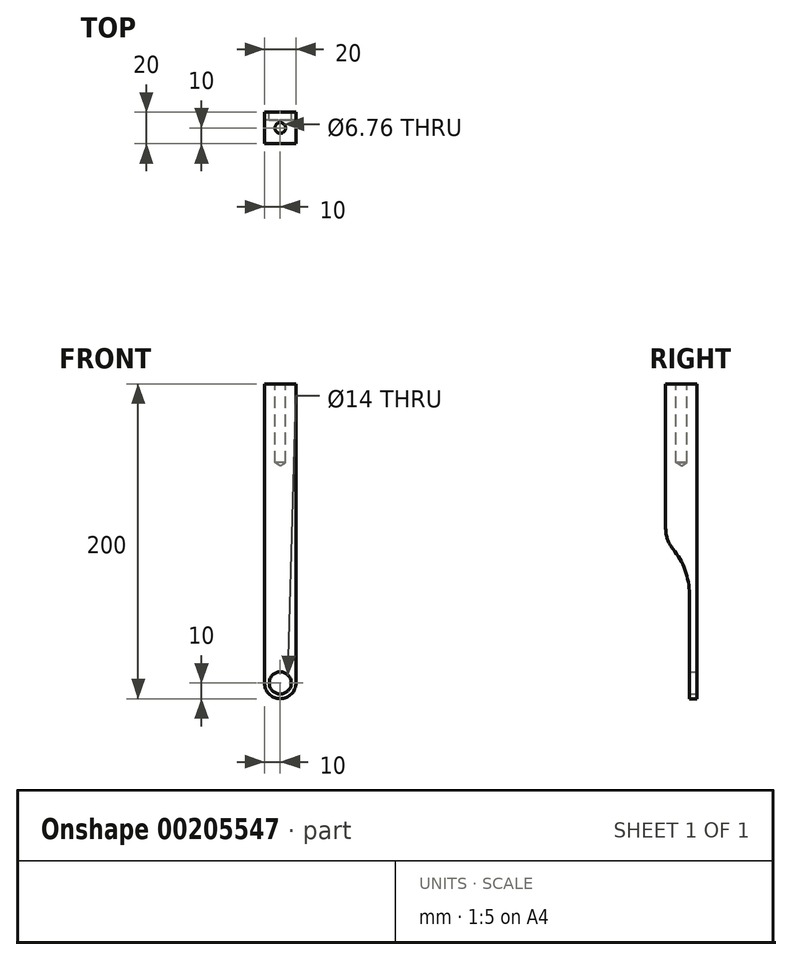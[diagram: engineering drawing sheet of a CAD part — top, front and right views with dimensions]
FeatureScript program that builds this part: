
annotation { "Feature Type Name" : "Feature", "Feature Type Description" : "" }
export const myFeature = defineFeature(function(context is Context, id is Id, definition is map)
    precondition{}
    {
        {
            var Q0;
            Q0=qCreatedBy(makeId("Front.planeOp"),FACE);
            var sketch = newSketch(context, id + "F0", { "sketchPlane" : qUnion([Q0])});
            skLineSegment(sketch, "E0.bottom", {"start": v(0, 0) * mm, "end": v(20, 0) * mm});
            skLineSegment(sketch, "E0.top", {"start": v(0, 200) * mm, "end": v(20, 200) * mm});
            skLineSegment(sketch, "E0.left", {"start": v(0, 0) * mm, "end": v(0, 200) * mm});
            skLineSegment(sketch, "E0.right", {"start": v(20, 0) * mm, "end": v(20, 200) * mm});
            skSolve(sketch);
        }
        {
            var Q0;
            Q0=qSketchRegion(id+"F0",true);
            extrude(context, id + "F1", {"entities" : qUnion([Q0]), "depth" : 20 * mm});
        }
        {
            var Q0;
            Q0=makeQuery(id+"F1.opExtrude","SWEPT_FACE",FACE,{"disambiguationData":[OSD([sQuery(id+"F0.wireOp",EDGE,"E0.right")])]});
            var sketch = newSketch(context, id + "F2", { "sketchPlane" : qUnion([Q0])});
            skLineSegment(sketch, "E1.bottom", {"start": v(-20, 0) * mm, "end": v(-5, 0) * mm});
            skLineSegment(sketch, "E1.top", {"start": v(-20, 100) * mm, "end": v(-5, 100) * mm});
            skLineSegment(sketch, "E1.left", {"start": v(-20, 0) * mm, "end": v(-20, 100) * mm});
            skLineSegment(sketch, "E1.right", {"start": v(-5, 0) * mm, "end": v(-5, 100) * mm});
            skSolve(sketch);
        }
        {
            var Q0;
            Q0=makeQuery(id+"F2.imprint","IMPRINT",FACE,{"disambiguationData":[TD([[makeQuery(id+"F2.imprint","IMPRINT",EDGE,{"derivedFrom":sQuery(id+"F2.wireOp",EDGE,"E1.bottom")}),1.0]])]});
            extrude(context, id + "F3", {"entities" : qUnion([Q0]), "operationType" : NewBodyOperationType.REMOVE, "oppositeDirection" : true, "depth" : 20 * mm});
        }
        {
            var Q0;
            Q0=makeQuery(id+"F1.opExtrude","CAP_FACE",FACE,{"disambiguationData":[OSD([sQuery(id+"F0.wireOp",EDGE,"E0.bottom"),sQuery(id+"F0.wireOp",EDGE,"E0.top"),sQuery(id+"F0.wireOp",EDGE,"E0.left"),sQuery(id+"F0.wireOp",EDGE,"E0.right")])],"isStart":true});
            var sketch = newSketch(context, id + "F4", { "sketchPlane" : qUnion([Q0])});
            skCircle(sketch, "E2", {"center": v(-10, 10) * mm, "radius": 10 * mm});
            skPoint(sketch, "E2.centerSnap0", {"position": v(-10, 0) * mm});
            skSolve(sketch);
        }
        {
            var Q0;
            {var subQ0=sQuery(id+"F4.wireOp",EDGE,"E2");var subQ1=makeQuery(id+"F1.opExtrude","CAP_EDGE",EDGE,{"disambiguationData":[OSD([sQuery(id+"F0.wireOp",EDGE,"E0.left")])],"isStart":true});var subQ2=makeQuery(id+"F4.imprint","INTERSECT",VERTEX,{"derivedFrom":[subQ1,subQ0]});Q0=makeQuery(id+"F4.imprint","IMPRINT",FACE,{"disambiguationData":[TD([[makeQuery(id+"F4.imprint","IMPRINT",EDGE,{"disambiguationData":[TD([[subQ2,1.0]])],"derivedFrom":subQ0}),-1.0]])]});}
            var Q1;
            {var subQ0=sQuery(id+"F4.wireOp",EDGE,"E2");var subQ1=makeQuery(id+"F1.opExtrude","CAP_EDGE",EDGE,{"disambiguationData":[OSD([sQuery(id+"F0.wireOp",EDGE,"E0.right")])],"isStart":true});var subQ2=makeQuery(id+"F4.imprint","INTERSECT",VERTEX,{"derivedFrom":[subQ1,subQ0]});Q1=makeQuery(id+"F4.imprint","IMPRINT",FACE,{"disambiguationData":[TD([[makeQuery(id+"F4.imprint","IMPRINT",EDGE,{"disambiguationData":[TD([[subQ2,-1.0]])],"derivedFrom":subQ0}),-1.0]])]});}
            var Q2;
            Q2=makeQuery(id+"F1.opExtrude","SWEPT_EDGE",EDGE,{"disambiguationData":[OSD([sQuery(id+"F0.wireOp",EDGE,"E0.bottom"),sQuery(id+"F0.wireOp",EDGE,"E0.left")])]});
            sweep(context, id + "F5", {"operationType" : NewBodyOperationType.REMOVE, "profiles" : qUnion([Q0, Q1]), "path" : qUnion([Q2])});
        }
        {
            var Q0;
            Q0=makeQuery(id+"F1.opExtrude","CAP_FACE",FACE,{"disambiguationData":[OSD([sQuery(id+"F0.wireOp",EDGE,"E0.bottom"),sQuery(id+"F0.wireOp",EDGE,"E0.top"),sQuery(id+"F0.wireOp",EDGE,"E0.left"),sQuery(id+"F0.wireOp",EDGE,"E0.right")])],"isStart":true});
            var sketch = newSketch(context, id + "F6", { "sketchPlane" : qUnion([Q0])});
            skCircle(sketch, "E3", {"center": v(-10, 10) * mm, "radius": 7 * mm});
            skSolve(sketch);
        }
        {
            var Q0;
            Q0=qSketchRegion(id+"F6",true);
            extrude(context, id + "F7", {"entities" : qUnion([Q0]), "operationType" : NewBodyOperationType.REMOVE, "endBound" : BoundingType.THROUGH_ALL, "oppositeDirection" : true, "depth" : 25 * mm});
        }
        {
            var Q0;
            Q0=makeQuery(id+"F3.boolean.opBoolean","COPY",EDGE,{"derivedFrom":makeQuery(id+"F3.opExtrude","SWEPT_EDGE",EDGE,{"disambiguationData":[OSD([sQuery(id+"F2.wireOp",EDGE,"E1.top"),sQuery(id+"F2.wireOp",EDGE,"E1.right")])]})});
            fillet(context, id + "F8", {"entities" : qUnion([Q0]), "radius" : 45 * mm, "tangentPropagation" : true, "allowEdgeOverflow" : false});
        }
        {
            var Q0;
            Q0=makeQuery(id+"F8.opFillet","BLEND_EDGE",EDGE,{"blendedFrom":[makeQuery(id+"F3.boolean.opBoolean","COPY",EDGE,{"derivedFrom":makeQuery(id+"F3.opExtrude","SWEPT_EDGE",EDGE,{"disambiguationData":[OSD([sQuery(id+"F2.wireOp",EDGE,"E1.top"),sQuery(id+"F2.wireOp",EDGE,"E1.right")])]})}),makeQuery(id+"F1.opExtrude","CAP_FACE",FACE,{"disambiguationData":[OSD([sQuery(id+"F0.wireOp",EDGE,"E0.bottom"),sQuery(id+"F0.wireOp",EDGE,"E0.top"),sQuery(id+"F0.wireOp",EDGE,"E0.left"),sQuery(id+"F0.wireOp",EDGE,"E0.right")])],"isStart":false})],"blendedInto":[makeQuery(id+"F1.opExtrude","CAP_FACE",FACE,{"disambiguationData":[OSD([sQuery(id+"F0.wireOp",EDGE,"E0.bottom"),sQuery(id+"F0.wireOp",EDGE,"E0.top"),sQuery(id+"F0.wireOp",EDGE,"E0.left"),sQuery(id+"F0.wireOp",EDGE,"E0.right")])],"isStart":false})]});
            fillet(context, id + "F9", {"entities" : qUnion([Q0]), "radius" : 20 * mm, "tangentPropagation" : true, "allowEdgeOverflow" : false});
        }
        {
            var Q0;
            Q0=makeQuery(id+"F1.opExtrude","SWEPT_FACE",FACE,{"disambiguationData":[OSD([sQuery(id+"F0.wireOp",EDGE,"E0.top")])]});
            var sketch = newSketch(context, id + "F10", { "sketchPlane" : qUnion([Q0])});
            skPoint(sketch, "E4", {"position": v(10, -10) * mm});
            skSolve(sketch);
        }
        {
            var Q0;
            Q0=sQuery(id+"F10.wireOp",VERTEX,"E4");
            var Q1;
            Q1=makeQuery(id+"F1.opExtrude","SWEPT_BODY",BODY,{"disambiguationData":[OSD([sQuery(id+"F0.wireOp",EDGE,"E0.bottom"),sQuery(id+"F0.wireOp",EDGE,"E0.top"),sQuery(id+"F0.wireOp",EDGE,"E0.left"),sQuery(id+"F0.wireOp",EDGE,"E0.right")])]});
            hole(context, id + "F11", {"style" : HoleStyle.SIMPLE, "endStyle" : HoleEndStyle.BLIND, "standardTappedOrClearance" : lookupTablePath({ "standard" : "ANSI", "fit" : "Normal (ASME)", "size" : "1/4", "type" : "Clearance" }), "standardBlindInLast" : lookupTablePath({ "fit" : "Free", "standard" : "ANSI", "size" : "1/4", "type" : "Clearance" }), "holeDiameter" : 6.76 * mm, "holeDepth" : 50 * mm, "locations" : qUnion([Q0]), "scope" : qUnion([Q1])});
        }
    });
